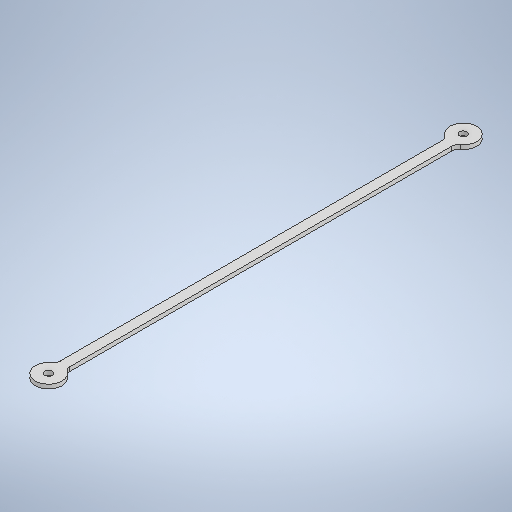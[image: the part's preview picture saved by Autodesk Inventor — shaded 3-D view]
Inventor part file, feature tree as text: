
AUTODESK INVENTOR PART (.ipt)
format: ipt  version: 2025.2 (Build 292293000, 293)  size: 282,112 bytes
history: native  units: in
note: dims shown in document units (in); Inventor stores cm internally (conversion verified against a paired STEP export)
features: extrude x2, sketch x2
ambient origin geometry x8: Origin, YZ Plane, XZ Plane, XY Plane, X Axis, Y Axis, Z Axis, Center Point
bodies: Solid1 (feature_tree)
feature tree (4):
  extrude  "Extrusion1"  Depth=0.1575in
  extrude  "Extrusion2"  Depth=0.0669in
  sketch  "Sketch1"  dims[d0=0.4291in d2=0.1575in]
  sketch  "Sketch2"  dims[d3=0.0787in d4=0.4291in d5=0.0787in d6=0.0in d7=6.6929in d8=0.2756in d9=0.2756in d10=0.0in d11=0.0669in d12=0.0in d13=0.1181in d14=0.1181in d15=0.0669in d16=0.0in]
